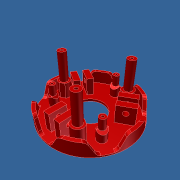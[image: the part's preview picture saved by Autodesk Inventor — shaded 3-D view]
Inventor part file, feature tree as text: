
AUTODESK INVENTOR PART (.ipt)
format: ipt  version: unknown  size: 482,304 bytes
history: native  units: mm
features: sketch x12, extrude x11, pattern_circular x4, fillet x1, chamfer x1, other x1, projected_geometry x1
ambient origin geometry x8: Origin, YZ Plane, XZ Plane, XY Plane, X Axis, Y Axis, Z Axis, Center Point
feature tree (31):
  extrude  "Выдавливание1"  Depth=15.6mm
  extrude  "Выдавливание2"  Depth=45.6mm
  extrude  "Выдавливание3"  Depth=2.0mm
  fillet  "Сопряжение1"  Radius=15.8mm
  pattern_circular  "Круговой массив2"  Count=3 Angle=360.0deg
  extrude  "Выдавливание4"  Depth=1.3mm TaperAngle=0.0deg
  extrude  "Выдавливание5"  Depth=1.6mm
  pattern_circular  "Круговой массив3"  [2 undecoded]
  chamfer  "Фаска1"  Distance=7.2mm
  extrude  "Выдавливание6"  Depth=14.0mm
  extrude  "Выдавливание7"  Depth=10.0mm TaperAngle=0.0deg
  extrude  "Выдавливание8"  Depth=2.0mm
  pattern_circular  "Круговой массив4"  Count=6 Angle=360.0deg
  extrude  "Выдавливание9"  Depth=6.0mm
  extrude  "Выдавливание10"  Depth=2.7mm
  sketch  "Эскиз11"
  other  "РабПлоскость1"
  extrude  "Выдавливание11"  Depth=7.8mm TaperAngle=0.0deg
  pattern_circular  "Круговой массив5"  [2 undecoded]
  sketch  "Эскиз1"
  sketch  "Эскиз2"
  sketch  "Эскиз3"
  sketch  "Эскиз4"
  sketch  "Эскиз5"
  sketch  "Эскиз6"
  projected_geometry  "Спроецированная петля1"
  sketch  "Эскиз7"
  sketch  "Эскиз8"
  sketch  "Эскиз9"
  sketch  "Эскиз10"
  sketch  "Эскиз12"
note: 4 required parameter values undecoded (feature->parameter linkage not recoverable at this tier; creation-order binding heuristic only, values carry confidence <= 0.55)
